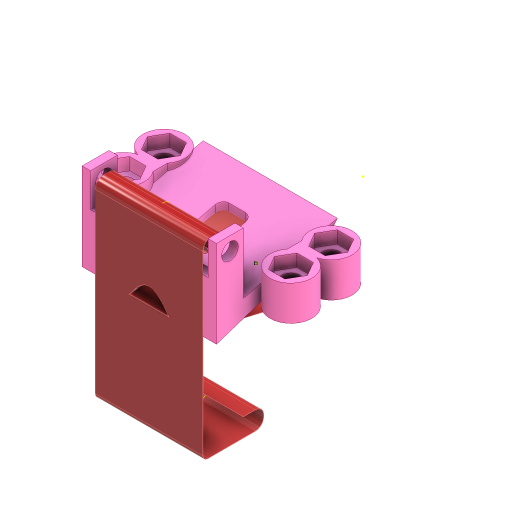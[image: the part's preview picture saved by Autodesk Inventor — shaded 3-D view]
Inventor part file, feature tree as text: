
AUTODESK INVENTOR PART (.ipt)
format: ipt  version: 2024 (Build 280153000, 153)  size: 1,720,832 bytes
history: native  units: mm
features: sketch x24, extrude x19, projected_geometry x11, split x10, other x10, loft x6, boolean_combine x5, plane x4, fillet x2, sweep x2, thicken_offset x2
ambient origin geometry x8: Origin, YZ Plane, XZ Plane, XY Plane, X Axis, Y Axis, Z Axis, Center Point
bodies: Solid1 (feature_tree), Solid2 (feature_tree), Solid19 (feature_tree), Solid20 (feature_tree), Solid21 (feature_tree), Solid22 (feature_tree), Solid23 (feature_tree), Solid3 (feature_tree), Solid4 (feature_tree), Solid5 (feature_tree), Solid6 (feature_tree), Solid7 (feature_tree), Solid8 (feature_tree), Solid9 (feature_tree), Solid10 (feature_tree), Solid11 (feature_tree), Solid12 (feature_tree), Solid13 (feature_tree), Solid14 (feature_tree), Solid15 (feature_tree), Solid16 (feature_tree), Solid17 (feature_tree), Solid18 (feature_tree)
feature tree (95):
  extrude  "Extrusion1"  Depth=3.0mm TaperAngle=0.0deg
  extrude  "Extrusion2"  Depth=3.0mm TaperAngle=0.0deg
  extrude  "Extrusion3"  Depth=40.0mm
  plane  "Work Plane2"
  sketch  "Sketch4"  dims[d4=29.0mm d5=3.0mm d6=0.0mm]
  loft  "Loft1"
  loft  "Loft2"
  loft  "Loft3"
  loft  "Loft4"
  boolean_combine  "Combine1"
  loft  "Loft5"
  fillet  "Fillet1"  [1 undecoded]
  fillet  "Fillet2"  [1 undecoded]
  plane  "Work Plane3"
  extrude  "Extrusion5"  TaperAngle=0.0deg  [1 undecoded]
  extrude  "Extrusion6"  TaperAngle=0.0deg  [1 undecoded]
  extrude  "Extrusion7"  Depth=40.0mm
  extrude  "Extrusion8"  TaperAngle=0.0deg  [1 undecoded]
  extrude  "Extrusion9"  Depth=2.0mm
  extrude  "Extrusion10"  Depth=38.0mm
  extrude  "Extrusion11"  Depth=3.0mm TaperAngle=0.0deg
  extrude  "Extrusion12"  Depth=3.0mm TaperAngle=0.0deg
  extrude  "Extrusion13"  Depth=12.5mm TaperAngle=0.0deg
  extrude  "Extrusion14"  Depth=3.7mm TaperAngle=0.0deg
  extrude  "Extrusion15"  Depth=8.5mm
  split  "Split1"
  split  "Split2"
  split  "Split3"
  split  "Split4"
  split  "Split5"
  split  "Split6"
  split  "Split7"
  boolean_combine  "Combine2"
  split  "Split8"
  boolean_combine  "Combine3"
  boolean_combine  "Combine4"
  extrude  "Extrusion16"  Depth=8.5mm
  extrude  "Extrusion17"  Depth=2.7mm TaperAngle=0.0deg
  sketch  "Sketch36"  dims[d47=15.0mm d48=3.0mm d49=0.0mm]
  sweep  "Sweep1"
  split  "Split9"
  loft  "Loft6"
  thicken_offset  "Thicken1"
  extrude  "Extrusion18"  Depth=10.0mm TaperAngle=0.0deg
  sweep  "Sweep2"
  split  "Split10"
  thicken_offset  "Thicken2"
  boolean_combine  "Combine5"
  plane  "Work Plane4"
  extrude  "Extrusion19"  Depth=10.0mm
  other  "Work Point1"
  other  "Work Point2"
  other  "Work Point3"
  extrude  "Extrusion20"  Depth=10.0mm
  sketch  "Sketch1"  dims[d0=3.0mm d1=0.0mm d2=9.5mm d3=0.0mm]
  plane  "Work Plane1"
  other  "2D Equation Curve1"
  other  "Edges1"
  other  "Edges2"
  other  "Edges3"
  other  "Edges4"
  sketch  "Sketch7"  dims[d7=12.0mm d8=36.0mm d9=40.0mm]
  sketch  "Sketch10"  dims[d10=9.0mm d11=10.0mm]
  sketch  "Sketch12"  dims[d12=3.0mm d13=-6.0mm d14=6.0mm]
  sketch  "Sketch13"  dims[d15=40.0mm d16=26.0mm]
  sketch  "Sketch16"  dims[d17=20.0mm d18=20.0mm]
  projected_geometry  "Projected Loop1"
  sketch  "Sketch18"  dims[d19=0.0mm d20=90.0deg d21=0.0mm d22=90.0deg d23=0.0mm d24=90.0deg d25=0.0mm d26=90.0deg]
  sketch  "Sketch19"  dims[d27=0.0mm d28=90.0deg d29=0.0mm d30=90.0deg]
  projected_geometry  "Projected Loop2"
  projected_geometry  "Projected Loop3"
  projected_geometry  "Projected Loop4"
  projected_geometry  "Projected Loop5"
  sketch  "Sketch23"  dims[d31=0.0mm d32=90.0deg d33=0.0mm d34=90.0deg]
  sketch  "Sketch24"  dims[d35=26.0mm d36=40.0mm]
  sketch  "Sketch28"  dims[d37=4.0mm d38=0.0mm d39=90.0deg]
  sketch  "Sketch29"  dims[d40=0.0mm d41=90.0deg d42=2.0mm]
  sketch  "Sketch35"  dims[d43=1.5mm d46=38.0mm]
  projected_geometry  "Projected Loop11"
  sketch  "3D Sketch2"
  other  "Srf1"
  sketch  "Sketch38"  dims[d50=15.0mm d51=3.0mm d52=0.0mm]
  projected_geometry  "Projected Loop12"
  sketch  "Sketch42"  dims[d53=11.0mm d54=12.5mm d55=0.0mm]
  projected_geometry  "Projected Loop19"
  projected_geometry  "Projected Loop20"
  sketch  "Sketch43"  dims[d56=11.0mm d57=3.7mm d58=0.0mm]
  sketch  "Sketch46"  dims[d59=20.0mm d60=0.0mm d61=8.5mm]
  projected_geometry  "Projected Loop21"
  sketch  "3D Sketch3"
  sketch  "Sketch47"  dims[d62=8.5mm d63=8.5mm]
  projected_geometry  "Projected Loop22"
  sketch  "Sketch49"  dims[d64=8.5mm d65=2.7mm d66=0.0mm]
  sketch  "Sketch50"  dims[d67=40.0mm d68=10.0mm d69=2.7mm d70=0.0mm d71=2.5mm d72=0.0mm d73=2.5mm d74=0.0mm d75=9.0mm d76=2.0mm d77=0.0mm d78=0.0mm d79=7.0mm d80=5.5mm d81=8.5mm d82=8.5mm d83=2.5mm d84=0.0mm d85=2.5mm d86=0.0mm d87=0.5mm d88=0.0mm d89=0.0mm d91=10.0mm d92=10.0mm d93=0.1mm d94=0.0mm d95=16.0mm d96=2.5mm d97=4.0mm d98=2.5mm d99=2.5mm d100=5.0mm d101=5.0mm d102=2.5mm d103=2.5mm d104=2.5mm d105=2.5mm d106=0.0mm d107=0.0mm d108=2.5mm d109=2.5mm d110=0.0mm d111=90.0deg d112=0.0mm d113=90.0deg d114=0.1mm d115=0.1mm d116=0.1mm d117=0.0mm d118=15.0mm d119=3.0mm d120=1.6mm d121=1.5mm d122=16.5mm d125=5.5mm d126=2.5mm d127=2.5mm d128=0.0mm d129=0.0mm d130=0.1mm d131=0.1mm d132=58.25mm d133=6.0mm d134=16.0mm d135=0.0mm d136=12.0mm d137=12.0mm d138=12.0mm d139=12.0mm d140=10.0mm d141=0.0mm]
  other  "Unwrap1"
note: 5 required parameter values undecoded (feature->parameter linkage not recoverable at this tier; creation-order binding heuristic only, values carry confidence <= 0.55)
